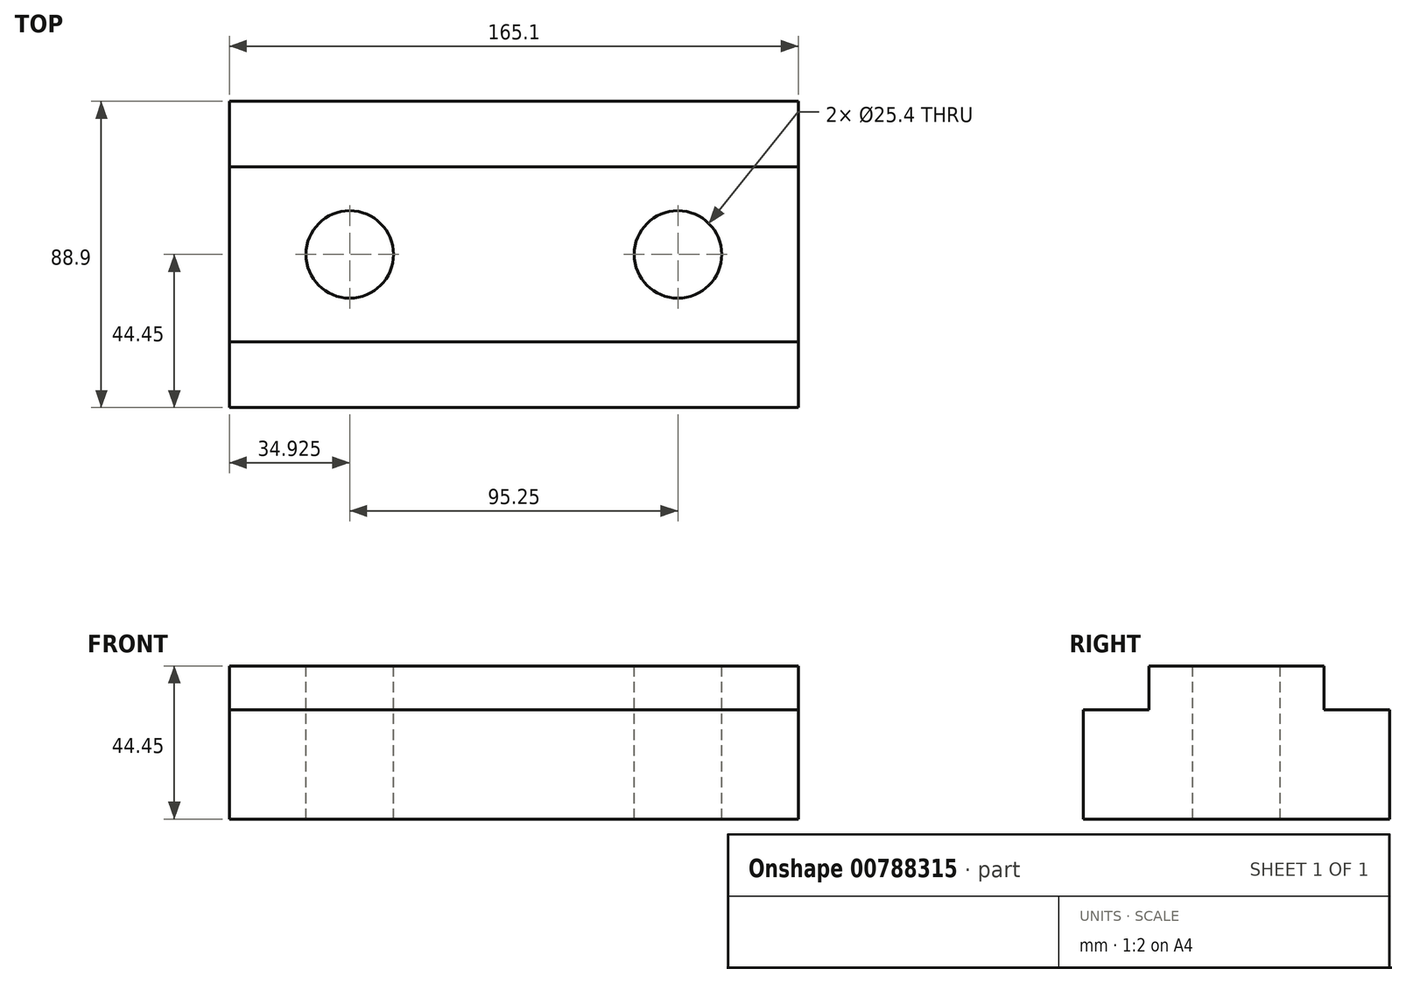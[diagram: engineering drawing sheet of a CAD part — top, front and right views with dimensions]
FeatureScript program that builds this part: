
annotation { "Feature Type Name" : "Feature", "Feature Type Description" : "" }
export const myFeature = defineFeature(function(context is Context, id is Id, definition is map)
    precondition{}
    {
        {
            var Q0;
            Q0=qCreatedBy(makeId("Right.planeOp"),FACE);
            var sketch = newSketch(context, id + "F0", { "sketchPlane" : qUnion([Q0])});
            skLineSegment(sketch, "E0", {"start": v(0, 0) * mm, "end": v(-19.05, 0) * mm});
            skLineSegment(sketch, "E1", {"start": v(-19.05, 0) * mm, "end": v(-19.05, 31.75) * mm});
            skLineSegment(sketch, "E2", {"start": v(-19.05, 31.75) * mm, "end": v(0, 31.75) * mm});
            skLineSegment(sketch, "E3", {"start": v(0, 31.75) * mm, "end": v(0, 44.45) * mm});
            skLineSegment(sketch, "E4", {"start": v(0, 44.45) * mm, "end": v(50.8, 44.45) * mm});
            skLineSegment(sketch, "E5", {"start": v(50.8, 44.45) * mm, "end": v(50.8, 31.75) * mm});
            skLineSegment(sketch, "E6", {"start": v(50.8, 31.75) * mm, "end": v(69.85, 31.75) * mm});
            skLineSegment(sketch, "E7", {"start": v(69.85, 31.75) * mm, "end": v(69.85, 0) * mm});
            skLineSegment(sketch, "E8", {"start": v(69.85, 0) * mm, "end": v(0, 0) * mm});
            skSolve(sketch);
        }
        {
            var Q0;
            Q0=makeQuery(id+"F0.imprint","IMPRINT",FACE,{"disambiguationData":[TD([[makeQuery(id+"F0.imprint","IMPRINT",EDGE,{"derivedFrom":sQuery(id+"F0.wireOp",EDGE,"E0")}),-1.0]])]});
            extrude(context, id + "F1", {"entities" : qUnion([Q0]), "depth" : 165.1 * mm, "offsetDistance" : 25.4 * mm});
        }
        {
            var Q0;
            Q0=makeQuery(id+"F1.opExtrude","SWEPT_FACE",FACE,{"disambiguationData":[OSD([sQuery(id+"F0.wireOp",EDGE,"E4")])]});
            var sketch = newSketch(context, id + "F2", { "sketchPlane" : qUnion([Q0])});
            skLineSegment(sketch, "E9", {"start": v(0, 25.4) * mm, "end": v(34.93, 25.4) * mm});
            skLineSegment(sketch, "E10", {"start": v(34.93, 25.4) * mm, "end": v(130.18, 25.4) * mm});
            skLineSegment(sketch, "E11", {"start": v(130.18, 25.4) * mm, "end": v(165.1, 25.4) * mm});
            skCircle(sketch, "E12", {"center": v(34.93, 25.4) * mm, "radius": 12.7 * mm});
            skCircle(sketch, "E13", {"center": v(130.18, 25.4) * mm, "radius": 12.7 * mm});
            skSolve(sketch);
        }
        {
            var Q0;
            {var subQ0=sQuery(id+"F2.wireOp",EDGE,"E10");var subQ1=sQuery(id+"F2.wireOp",EDGE,"E9");var subQ2=makeQuery(id+"F2.imprint","INTERSECT",VERTEX,{"derivedFrom":[subQ1,subQ0]});Q0=makeQuery(id+"F2.imprint","IMPRINT",FACE,{"disambiguationData":[TD([[makeQuery(id+"F2.imprint","IMPRINT",EDGE,{"disambiguationData":[TD([[subQ2,1.0]])],"derivedFrom":subQ1}),-1.0]])]});}
            var Q1;
            {var subQ0=sQuery(id+"F2.wireOp",EDGE,"E11");var subQ1=sQuery(id+"F2.wireOp",EDGE,"E10");var subQ2=makeQuery(id+"F2.imprint","INTERSECT",VERTEX,{"derivedFrom":[subQ1,subQ0]});Q1=makeQuery(id+"F2.imprint","IMPRINT",FACE,{"disambiguationData":[TD([[makeQuery(id+"F2.imprint","IMPRINT",EDGE,{"disambiguationData":[TD([[subQ2,1.0]])],"derivedFrom":subQ1}),1.0]])]});}
            var Q2;
            {var subQ0=sQuery(id+"F2.wireOp",EDGE,"E11");var subQ1=sQuery(id+"F2.wireOp",EDGE,"E10");var subQ2=makeQuery(id+"F2.imprint","INTERSECT",VERTEX,{"derivedFrom":[subQ1,subQ0]});Q2=makeQuery(id+"F2.imprint","IMPRINT",FACE,{"disambiguationData":[TD([[makeQuery(id+"F2.imprint","IMPRINT",EDGE,{"disambiguationData":[TD([[subQ2,1.0]])],"derivedFrom":subQ1}),-1.0]])]});}
            var Q3;
            {var subQ0=sQuery(id+"F2.wireOp",EDGE,"E10");var subQ1=sQuery(id+"F2.wireOp",EDGE,"E9");var subQ2=makeQuery(id+"F2.imprint","INTERSECT",VERTEX,{"derivedFrom":[subQ1,subQ0]});Q3=makeQuery(id+"F2.imprint","IMPRINT",FACE,{"disambiguationData":[TD([[makeQuery(id+"F2.imprint","IMPRINT",EDGE,{"disambiguationData":[TD([[subQ2,1.0]])],"derivedFrom":subQ1}),1.0]])]});}
            extrude(context, id + "F3", {"entities" : qUnion([Q0, Q1, Q2, Q3]), "operationType" : NewBodyOperationType.REMOVE, "endBound" : BoundingType.UP_TO_NEXT, "oppositeDirection" : true, "depth" : 25.4 * mm, "offsetDistance" : 25.4 * mm});
        }
    });
